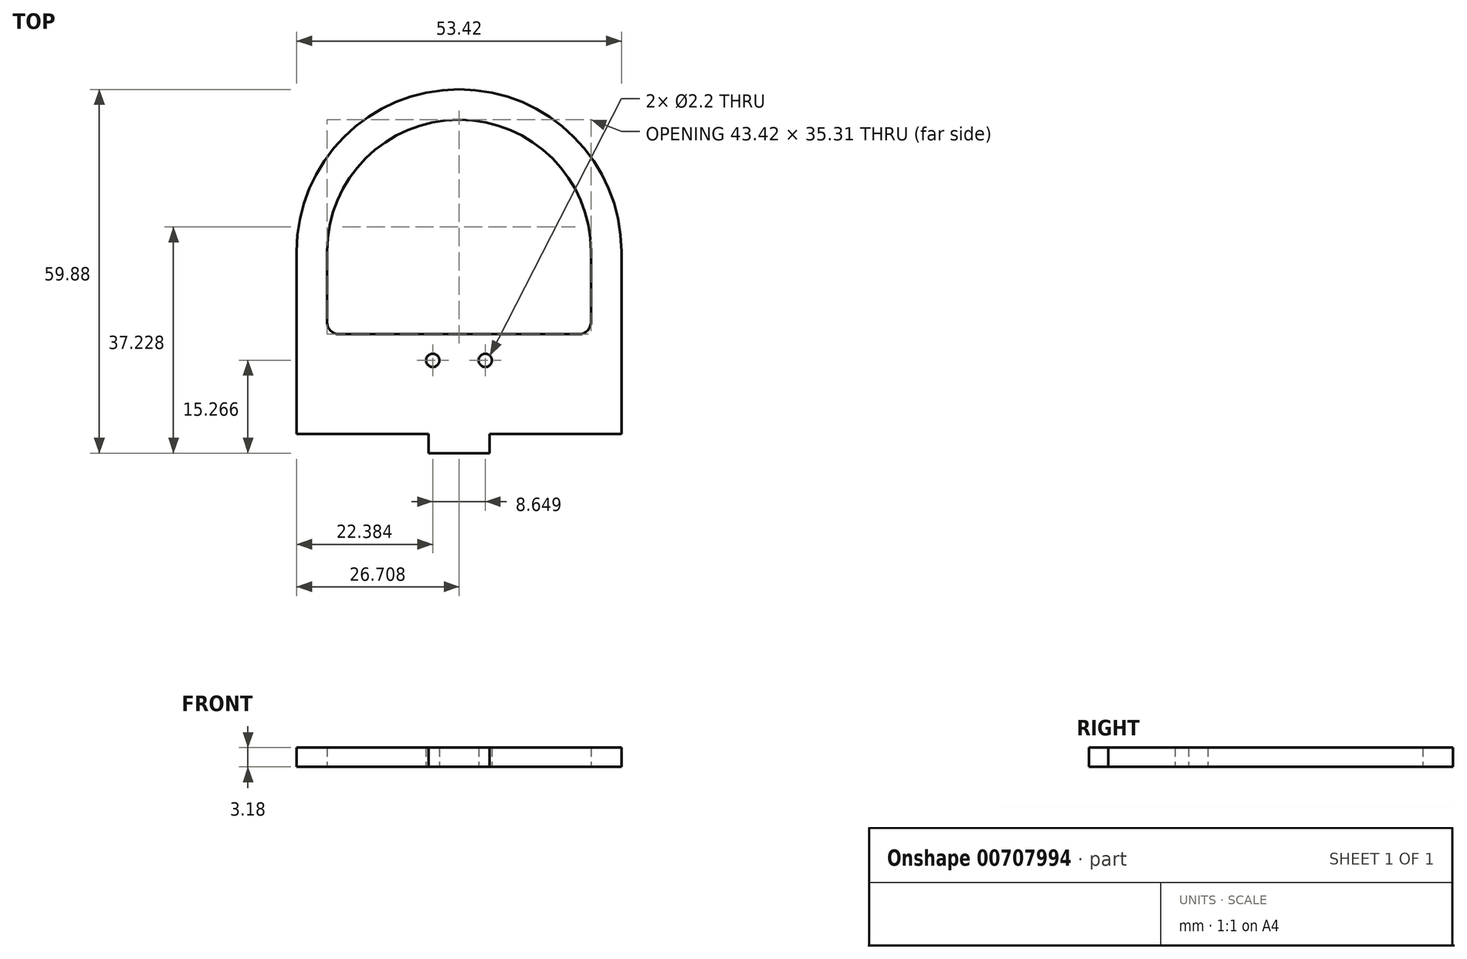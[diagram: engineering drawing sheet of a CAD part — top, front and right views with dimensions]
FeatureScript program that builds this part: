
annotation { "Feature Type Name" : "Feature", "Feature Type Description" : "" }
export const myFeature = defineFeature(function(context is Context, id is Id, definition is map)
    precondition{}
    {
        {
            var Q0;
            Q0=qCreatedBy(makeId("Top.planeOp"), FACE);
            var sketch = newSketch(context, id + "F0", { "sketchPlane" : qUnion([Q0])});
            skPoint(sketch, "E0.0", {"position": v(25.24, -9.39) * mm});
            skPoint(sketch, "E1.0", {"position": v(-6.47, -9.39) * mm});
            skPoint(sketch, "E2.0", {"position": v(3.53, -9.39) * mm});
            skPoint(sketch, "E3.0", {"position": v(-28.18, -9.39) * mm});
            skLineSegment(sketch, "E4", {"start": v(-28.18, -9.39) * mm, "end": v(-6.47, -9.39) * mm});
            skLineSegment(sketch, "E5", {"start": v(-6.47, -12.56) * mm, "end": v(3.53, -12.56) * mm});
            skLineSegment(sketch, "E6", {"start": v(3.53, -12.56) * mm, "end": v(3.53, -9.39) * mm});
            skLineSegment(sketch, "E7", {"start": v(3.53, -9.39) * mm, "end": v(25.24, -9.39) * mm});
            skLineSegment(sketch, "E8", {"start": v(-6.47, -9.39) * mm, "end": v(-6.47, -12.56) * mm});
            skLineSegment(sketch, "E9", {"start": v(-28.18, -9.39) * mm, "end": v(-28.18, 20.61) * mm});
            skLineSegment(sketch, "E10", {"start": v(25.24, 20.61) * mm, "end": v(25.24, -9.39) * mm});
            skArc(sketch, "E11", {"start": v(25.24, 20.61) * mm, "mid": v(-1.47, 47.32) * mm, "end": v(-28.18, 20.61) * mm});
            skLineSegment(sketch, "E12.1", {"start": v(20.24, 20.61) * mm, "end": v(20.24, 9.01) * mm});
            skArc(sketch, "E12.2", {"start": v(20.24, 20.61) * mm, "mid": v(-1.47, 42.32) * mm, "end": v(-23.18, 20.61) * mm});
            skLineSegment(sketch, "E12.3", {"start": v(-23.18, 9.01) * mm, "end": v(-23.18, 20.61) * mm});
            skLineSegment(sketch, "E13", {"start": v(-21.18, 7.01) * mm, "end": v(18.24, 7.01) * mm});
            skPoint(sketch, "E14.orphan", {"position": v(20.24, -6.59) * mm});
            skPoint(sketch, "E15.orphan", {"position": v(-23.18, -6.59) * mm});
            skPoint(sketch, "E16.visualSharp", {"position": v(-23.18, 7.01) * mm});
            skArc(sketch, "E16.filletArc", {"start": v(-23.18, 9.01) * mm, "mid": v(-22.6, 7.6) * mm, "end": v(-21.18, 7.01) * mm});
            skPoint(sketch, "E17.visualSharp", {"position": v(20.24, 7.01) * mm});
            skArc(sketch, "E17.filletArc", {"start": v(18.24, 7.01) * mm, "mid": v(19.65, 7.6) * mm, "end": v(20.24, 9.01) * mm});
            skCircle(sketch, "E18", {"center": v(-5.8, 2.7) * mm, "radius": 1.1 * mm});
            skLineSegment(sketch, "E19", {"start": v(-1.47, 7.01) * mm, "end": v(-1.47, 0.1) * mm, "construction": true});
            skCircle(sketch, "E20.MirrorC", {"center": v(2.85, 2.7) * mm, "radius": 1.1 * mm});
            skSolve(sketch);
        }
        {
            var Q0;
            Q0 = qSketchRegion(id + "F0", true);
            extrude(context, id + "F1", {"entities" : qUnion([Q0]), "depth" : 3.17 * mm, "offsetDistance" : 25 * mm});
        }
    });
